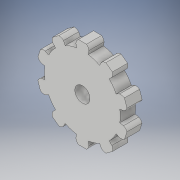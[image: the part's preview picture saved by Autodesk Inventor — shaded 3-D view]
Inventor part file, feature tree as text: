
AUTODESK INVENTOR PART (.ipt)
format: ipt  version: 2017 (Build 210142000, 142)  size: 185,856 bytes
history: native  units: in
note: dims shown in document units (in); Inventor stores cm internally (conversion verified against a paired STEP export)
features: extrude x2, sketch x2, pattern_circular x1
ambient origin geometry x8: Origin, YZ Plane, XZ Plane, XY Plane, X Axis, Y Axis, Z Axis, Center Point
bodies: Solid1 (feature_tree)
feature tree (5):
  extrude  "Extrusion1"  Depth=0.075in
  pattern_circular  "Circular Pattern1"  [2 undecoded]
  extrude  "Extrusion2"  Depth=0.15in TaperAngle=360.0deg
  sketch  "Sketch1"  dims[d0=0.75in d1=0.075in]
  sketch  "Sketch2"  dims[d2=0.04in d3=0.04in d4=15.748in d6=360.0deg d8=0.062in d9=0.062in d10=0.15in d11=0.0in d12=3.937in d13=360.0deg d15=0.15in d16=0.15in d17=0.0in]
note: 2 required parameter values undecoded (feature->parameter linkage not recoverable at this tier; creation-order binding heuristic only, values carry confidence <= 0.55)
